# Revit family: Deca_Acabamento para registro de gaveta de 1 ¼'' e 1 ½''_Unic_4900.90.GD
name_source: partatom
category: Plumbing Fixtures
units: mm (PartAtom-declared; Revit-internal decimal feet)

## family parameters
Cut with Voids When Loaded = No
Host = Face
Part Type = Normal
Room Calculation Point = No
Round Connector Dimension = Use Radius
Shared = No

## types (5) — shared parameters
Acompanha o Produto = -
Aprovado por = quattroD
Atendimento ao Cliente = 0800-0117073
CW Connection = No
Categoria = METAIS PARA BANHEIRO
Composição Anel Vedação = -
Composição Assento = -
Composição Básica = Liga de Cobre (bronze e latão),Plásticos de Engenharia
Composição Componente = -
Consumo = -
Cor Interna = -
Cor Secundária = -
Cores Componente = -
Criado por = quattroD
Código Pai = 4900.90.GD
Default Elevation = 1800 mm
Description = Acabamento para registro de gaveta de 1 1/4" e 1 1/2"
Informações Complementares = -
Itens de Instalação = -
Linha = Unic
Manufacturer = Deca
Norma = Não Possui
Pressão máx. funcionamento = -
Pressão mín. Aquec. Acúmulo = -
Pressão mín. Aquec. Passagem = -
Pressão mín. funcionamento = -
Saída de Esgoto = -
Segmento = Banheiro Luxo
Tipo de dispositivo economizador = -
Tipo de mecanismo utilizado = -
Tipo de rosca de entrada = -
Tipo de rosca de saída = -
URL = www.deca.com.br
Vazão na Pressão máx. (L/min) = -
Vazão na Pressão mín. (L/min) = -
zero-valued in all types: CWFU

## per-type parameters (varying)
| type | Cor Principal | Material | Model | Peso Líquido (Kg) |
| 4900.C90.GD_Cromado | Cromado | Deca_Cromado | 4900.C90.GD | 0.976 |
| 4900.BL90.GD.MT_Black Matte | Black Matte | Deca_Black Matte | 4900.BL90.GD.MT | 0.976 |
| 4900.CT90.GD.MT_Corten | Corten | Deca_Corten | 4900.CT90.GD.MT | 0.976 |
| 4900.GL90.GD.MT_Gold Matte | Gold Matte | Deca_Gold Matte | 4900.GL90.GD.MT | 0.976 |
| 4900.GL90.GD.RD_Red Gold | Red Gold | Deca_Red Gold | 4900.GL90.GD.RD | 0.945 |

## geometry (parser evidence)
native form markers: Sweep x2
no freeform markers — native parametric forms only
